# Revit family: CONV_Zero_GnrlPrpseLmnrs_ConvexSpotlight
name_source: partatom
category: Lighting Fixtures
revit_build: Autodesk Revit 2016 (Build: 20150714_1515(x64)
units: mm (PartAtom-declared; Revit-internal decimal feet)

## family parameters
Cut with Voids When Loaded = No
Host = Face
Light Source = Yes
OmniClass Number = 23.80.70.00
OmniClass Title = Lighting
Part Type = Normal
Room Calculation Point = No
Round Connector Dimension = Use Diameter
Shared = No

## types (6) — shared parameters
AssetType = Fixed
BIMObjectName = CONV_Zero_GnrlPrpseLmnrs_ConvexSpotlight
Brand = Zero
Category = Wall
Collection = Convex
Color = Various
Color Filter = 16777215
ConvergoRefNr = 0046-1708-0006-SE
Dimming Lamp Color Temperature Shift = <None>
DurationUnit = Year
Emit Shape Visible in Rendering = No
Features = Terminalblock
Finish = Painted aluminum
HasProtectiveEarth = No
IP_Code = IP20
IfcExportAs = IfcLightFixtureType
IfcExportType = NOTDEFINED
LensMaterial = Tempered glass
LightFixtureMountingType = Surface
LightFixturePlacingType = Wall/ceiling
Manufacturer = Zero
ManufacturerName = Zero
ManufacturerURL = https://www.zerolighting.com
Material = Metal
NBSDescription = General purpose luminaires
NBSReference = 90-60-50/405
Name = GnrlPrpseLmnrs_ConvexSpotlight
NominalCurrent = 0 A
NominalDiameter = 124 mm  [stored 0.406824 ft]
NominalFrequencyRange = 50 Hz
NominalHeight = 254 mm
NominalLength = 124 mm  [stored 0.406824 ft]
NominalRadius = 62 mm  [stored 0.203412 ft]
NominalVoltage = 230 V
NominalVoltageCalc = 0 V
NominalWidth = 124 mm  [stored 0.406824 ft]
NumberOfPoles = 1
PhaseAngle = 0.00°
Revision = 1
Shape = Sculptured
Size = 124x124x254 mm
TotalWattage = 17 W
URL = https://www.zerolighting.com
Uniclass2 = Pr_70_70_49
Uniclass2015Description = Surface luminaires
Uniclass2015Reference = Pr_70_70_48_85
UsageCurrent = 0 A
Version = 1
VersionDate = 13/12/2017
WarrantyDurationUnit = Year
zero-valued in all types: Default Elevation, ElectricalDeviceNominalPower, MaintenanceFactor, NumberOfSources

## per-type parameters (varying)
| type | ArticleNumber | Dimming | Emit from Circle Diameter | ModelNumber | Note | Photometric Web File | Tilt Angle |
| Convex spotlight LED1325LM/17W narrow beam | 8400-1-XX | None | 610 mm | 8400-1-XX |  | Convex8400-8405_IES.IES | 0.00° |
| Convex spotlight LED1325LM/17W medium beam | 8401-1-XX | None | 610 mm | 8401-1-XX | Article numbers change according shade colors.  XX = -01 White, -06 Black, -11 Grey, -12 Green. | Convex8401-8406_IES.IES | 0.00° |
| Convex spotlight LED1325LM/17W wide beam | 8402-1-XX | None | 610 mm | 8402-1-XX | Article numbers change according shade colors.  XX = -01 White, -06 Black, -11 Grey, -12 Green. | Convex8402-8407_IES.IES | 0.00° |
| Convex spotlight LED1325LM/17W HFF wide beam | 8402-1-XXHFF | Dimmbart DALI alt. SwitchDim/Dimmable DALI or SwitchDim | 610 mm | 8402-1-XXHFF | Article numbers change according shade colors.  XX = -01 White, -06 Black, -11 Grey, -12 Green. | Convex8402-8407_IES.IES | 0.00° |
| Convex spotlight LED1325LM/17W HFF medium beam | 8401-1-XXHFF | Dimmbart DALI alt. SwitchDim/Dimmable DALI or SwitchDim | 122 mm  [stored 0.400262 ft] | 8401-1-XXHFF | Article numbers change according shade colors.  XX = -01 White, -06 Black, -11 Grey, -12 Green. | Convex8401-8406_IES.IES | 90.00° |
| Convex spotlight LED1325LM/17W HFF narrow beam | 8400-1-XXHFF | Dimmbart DALI alt. SwitchDim/Dimmable DALI or SwitchDim | 610 mm | 8400-1-XXHFF |  | Convex8400-8405_IES.IES | 0.00° |

note: column(s) folded — value = type name in every type: Model

note: [stored X ft] marks values corroborated as IEEE doubles in the binary element streams (Revit-internal decimal feet)

## geometry (parser evidence)
native form markers: Sweep x5
no freeform markers — native parametric forms only
